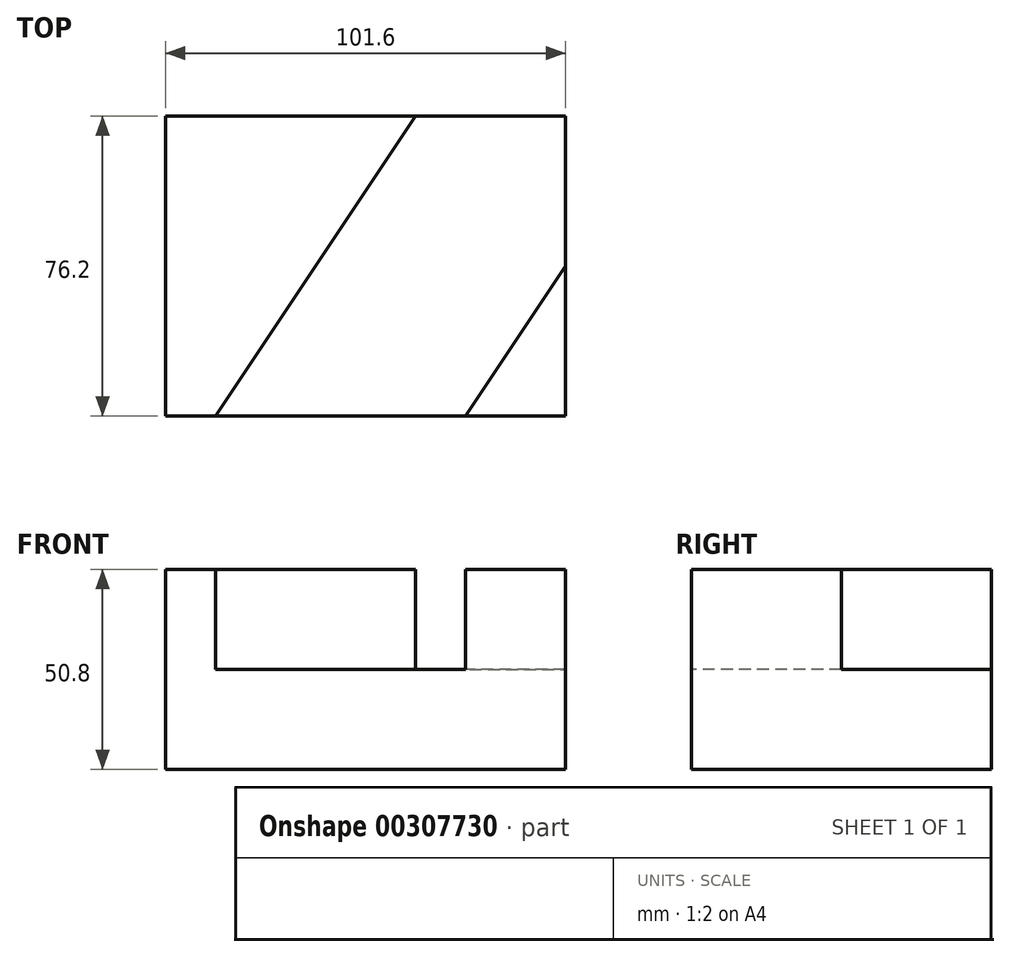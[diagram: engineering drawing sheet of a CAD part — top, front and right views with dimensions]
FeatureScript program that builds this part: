
annotation { "Feature Type Name" : "Feature", "Feature Type Description" : "" }
export const myFeature = defineFeature(function(context is Context, id is Id, definition is map)
    precondition{}
    {
        {
            var Q0;
            Q0=qCreatedBy(makeId("Top.planeOp"),FACE);
            var sketch = newSketch(context, id + "F0", { "sketchPlane" : qUnion([Q0])});
            skLineSegment(sketch, "E0", {"start": v(43.37, 25.87) * mm, "end": v(43.37, -50.33) * mm});
            skLineSegment(sketch, "E1", {"start": v(43.37, -50.33) * mm, "end": v(-58.23, -50.33) * mm});
            skLineSegment(sketch, "E2", {"start": v(-58.23, -50.33) * mm, "end": v(-58.23, 25.87) * mm});
            skLineSegment(sketch, "E3", {"start": v(-58.23, 25.87) * mm, "end": v(43.37, 25.87) * mm});
            skSolve(sketch);
        }
        {
            var Q0;
            Q0=makeQuery(id+"F0.imprint","IMPRINT",FACE,{"disambiguationData":[TD([[makeQuery(id+"F0.imprint","IMPRINT",EDGE,{"derivedFrom":sQuery(id+"F0.wireOp",EDGE,"E0")}),-1.0]])]});
            extrude(context, id + "F1", {"entities" : qUnion([Q0]), "depth" : 25.4 * mm});
        }
        {
            var Q0;
            Q0=makeQuery(id+"F1.opExtrude","CAP_FACE",FACE,{"disambiguationData":[OSD([sQuery(id+"F0.wireOp",EDGE,"E0"),sQuery(id+"F0.wireOp",EDGE,"E1"),sQuery(id+"F0.wireOp",EDGE,"E2"),sQuery(id+"F0.wireOp",EDGE,"E3")])],"isStart":false});
            var sketch = newSketch(context, id + "F2", { "sketchPlane" : qUnion([Q0])});
            skLineSegment(sketch, "E4", {"start": v(-45.53, -50.33) * mm, "end": v(-58.23, -50.33) * mm});
            skLineSegment(sketch, "E5", {"start": v(-58.23, -50.33) * mm, "end": v(-58.23, 25.87) * mm});
            skLineSegment(sketch, "E6", {"start": v(-58.23, 25.87) * mm, "end": v(5.27, 25.87) * mm});
            skLineSegment(sketch, "E7", {"start": v(5.27, 25.87) * mm, "end": v(-45.53, -50.33) * mm});
            skLineSegment(sketch, "E8", {"start": v(17.97, -50.33) * mm, "end": v(43.37, -50.33) * mm});
            skLineSegment(sketch, "E9", {"start": v(43.37, -50.33) * mm, "end": v(43.37, -12.23) * mm});
            skLineSegment(sketch, "E10", {"start": v(43.37, -12.23) * mm, "end": v(17.97, -50.33) * mm});
            skSolve(sketch);
        }
        {
            var Q0;
            Q0=makeQuery(id+"F2.imprint","IMPRINT",FACE,{"disambiguationData":[TD([[makeQuery(id+"F2.imprint","IMPRINT",EDGE,{"derivedFrom":sQuery(id+"F2.wireOp",EDGE,"E4")}),-1.0]])]});
            var Q1;
            Q1=makeQuery(id+"F2.imprint","IMPRINT",FACE,{"disambiguationData":[TD([[makeQuery(id+"F2.imprint","IMPRINT",EDGE,{"derivedFrom":sQuery(id+"F2.wireOp",EDGE,"E8")}),-1.0]])]});
            extrude(context, id + "F3", {"entities" : qUnion([Q0, Q1]), "operationType" : NewBodyOperationType.ADD, "depth" : 25.4 * mm});
        }
    });
